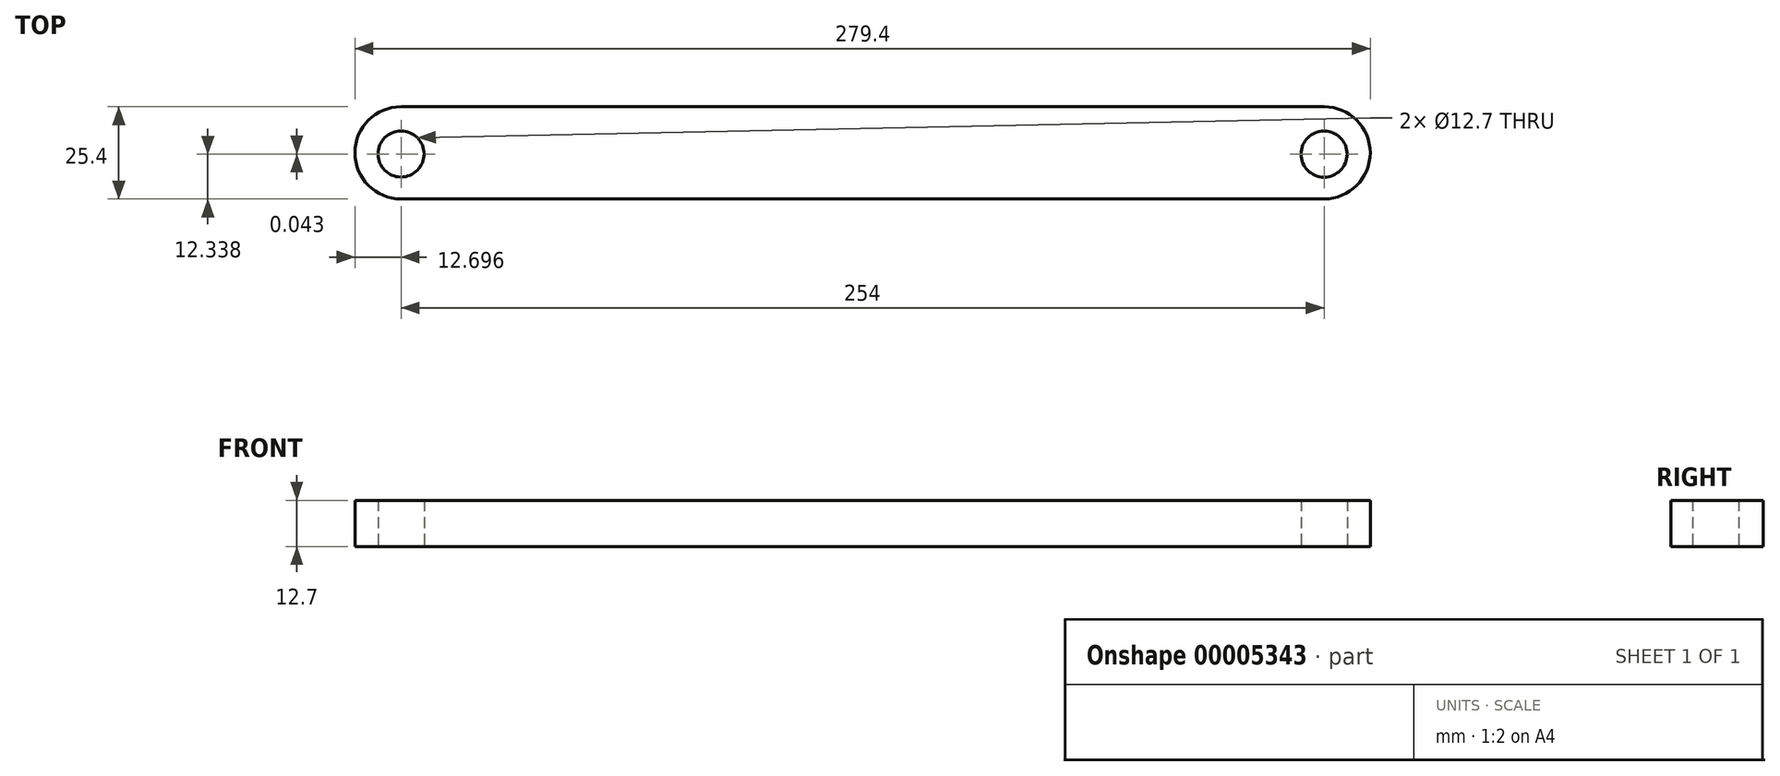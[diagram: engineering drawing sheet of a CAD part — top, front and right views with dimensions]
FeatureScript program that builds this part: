
annotation { "Feature Type Name" : "Feature", "Feature Type Description" : "" }
export const myFeature = defineFeature(function(context is Context, id is Id, definition is map)
    precondition{}
    {
        {
            var Q0;
            Q0=qCreatedBy(makeId("Top.planeOp"),FACE);
            var sketch = newSketch(context, id + "F0", { "sketchPlane" : qUnion([Q0])});
            skLineSegment(sketch, "E0.bottom", {"start": v(-115.84, -7.9) * mm, "end": v(138.16, -7.9) * mm});
            skLineSegment(sketch, "E0.top", {"start": v(-115.84, -33.3) * mm, "end": v(138.16, -33.3) * mm});
            skLineSegment(sketch, "E0.left", {"start": v(-115.84, -7.9) * mm, "end": v(-115.84, -33.3) * mm});
            skLineSegment(sketch, "E0.right", {"start": v(138.16, -7.9) * mm, "end": v(138.16, -33.3) * mm});
            skCircle(sketch, "E1", {"center": v(-115.84, -20.9) * mm, "radius": 6.35 * mm});
            skCircle(sketch, "E2", {"center": v(138.16, -20.95) * mm, "radius": 6.35 * mm});
            skArc(sketch, "E3", {"start": v(-115.84, -33.3) * mm, "mid": v(-128.54, -20.6) * mm, "end": v(-115.84, -7.9) * mm});
            skArc(sketch, "E4", {"start": v(138.16, -33.3) * mm, "mid": v(150.86, -20.6) * mm, "end": v(138.16, -7.9) * mm});
            skSolve(sketch);
        }
        {
            var Q0;
            Q0 = qSketchRegion(id + "F0", true);
            extrude(context, id + "F1", {"entities" : qUnion([Q0]), "depth" : 12.7 * mm});
        }
    });
